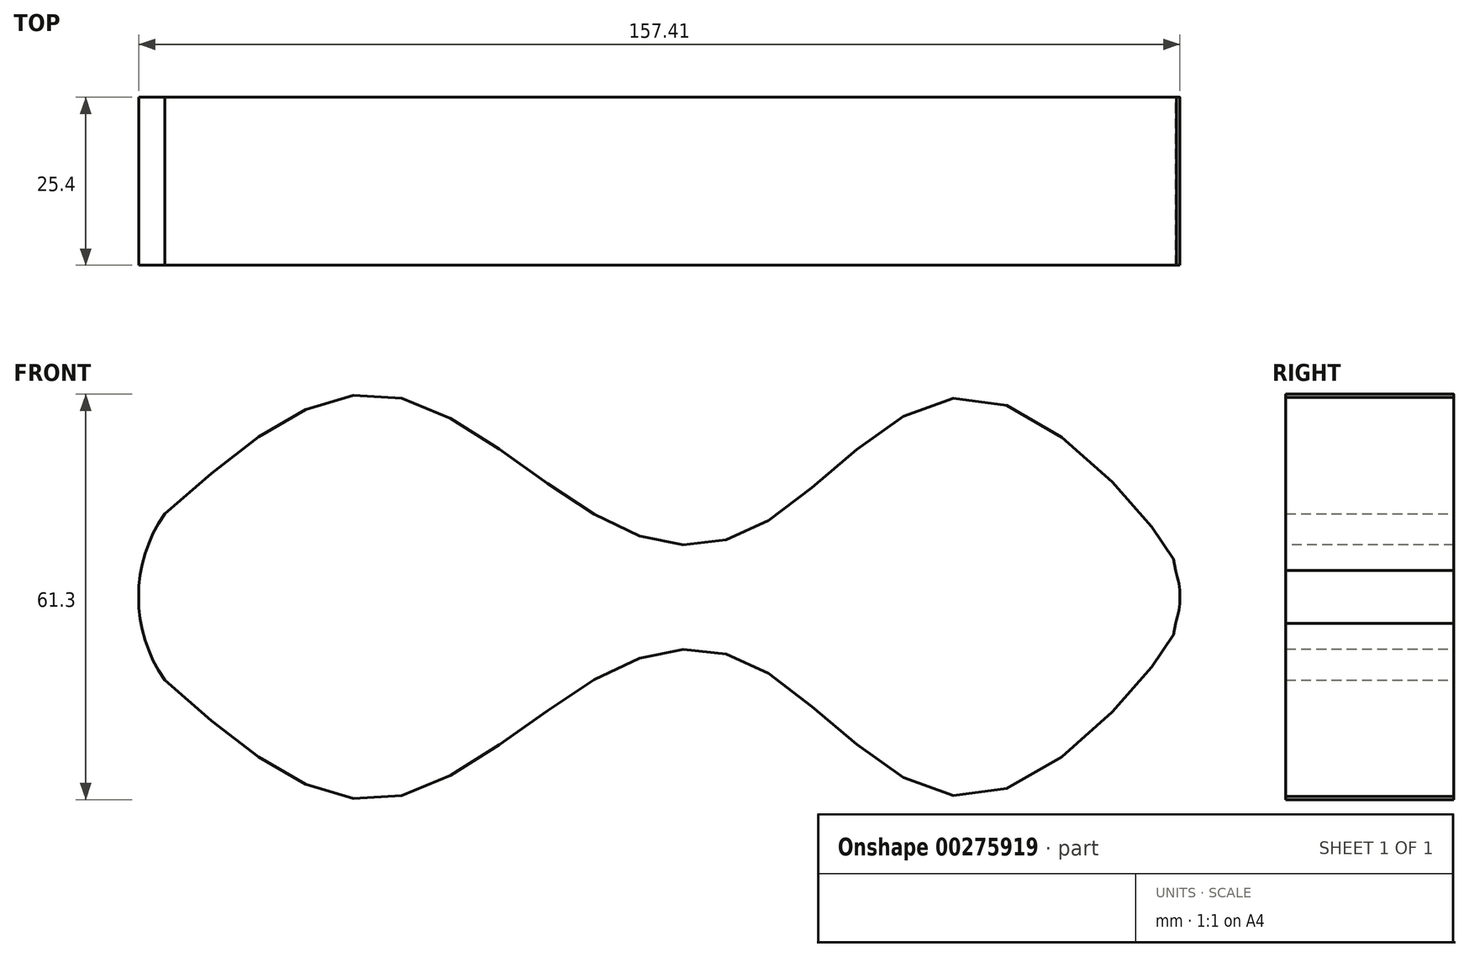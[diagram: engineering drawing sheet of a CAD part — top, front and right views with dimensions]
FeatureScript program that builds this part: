
annotation { "Feature Type Name" : "Feature", "Feature Type Description" : "" }
export const myFeature = defineFeature(function(context is Context, id is Id, definition is map)
    precondition{}
    {
        {
            var Q0;
            Q0=qCreatedBy(makeId("Front.planeOp"),FACE);
            var sketch = newSketch(context, id + "F0", { "sketchPlane" : qUnion([Q0])});
            skFitSpline(sketch, "E0", {"points": [v(-75.68, 12.57) * mm, v(-42.84, 30.56) * mm, v(-8.85, 11.42) * mm, v(15.42, 11.42) * mm, v(47.98, 29.99) * mm, v(77.1, 5.14) * mm, v(77.1, 4) * mm], "startDerivative": vector(162.73, 143.7) * mm, "endDerivative": vector(-11.5, -19.98) * mm});
            skFitSpline(sketch, "E1.MirrorCS", {"points": [v(-75.68, -12.57) * mm, v(-42.84, -30.56) * mm, v(-8.85, -11.42) * mm, v(15.42, -11.42) * mm, v(47.98, -29.99) * mm, v(77.1, -5.14) * mm, v(77.1, -4) * mm], "startDerivative": vector(162.73, -143.7) * mm, "endDerivative": vector(-11.5, 19.98) * mm});
            skArc(sketch, "E2", {"start": v(-75.68, 12.57) * mm, "mid": v(-79.61, 0) * mm, "end": v(-75.68, -12.57) * mm});
            skArc(sketch, "E3", {"start": v(77.1, -4) * mm, "mid": v(77.8, 0) * mm, "end": v(77.1, 4) * mm});
            skPoint(sketch, "E4", {"position": v(0, 0) * mm});
            skPoint(sketch, "E5", {"position": v(-44.61, 18.44) * mm});
            skPoint(sketch, "E6", {"position": v(46.64, 18.44) * mm});
            skPoint(sketch, "E7", {"position": v(46.64, -19.73) * mm});
            skPoint(sketch, "E8", {"position": v(-44.61, -19.73) * mm});
            skPoint(sketch, "E9", {"position": v(-44.61, -22.3) * mm});
            skPoint(sketch, "E10", {"position": v(-72.64, 0) * mm});
            skSolve(sketch);
        }
        {
            var Q0;
            Q0=makeQuery(id+"F0.imprint","IMPRINT",FACE,{"disambiguationData":[TD([[makeQuery(id+"F0.imprint","IMPRINT",EDGE,{"derivedFrom":sQuery(id+"F0.wireOp",EDGE,"E0")}),-1.0]])]});
            extrude(context, id + "F1", {"entities" : qUnion([Q0]), "depth" : 25.4 * mm});
        }
    });
